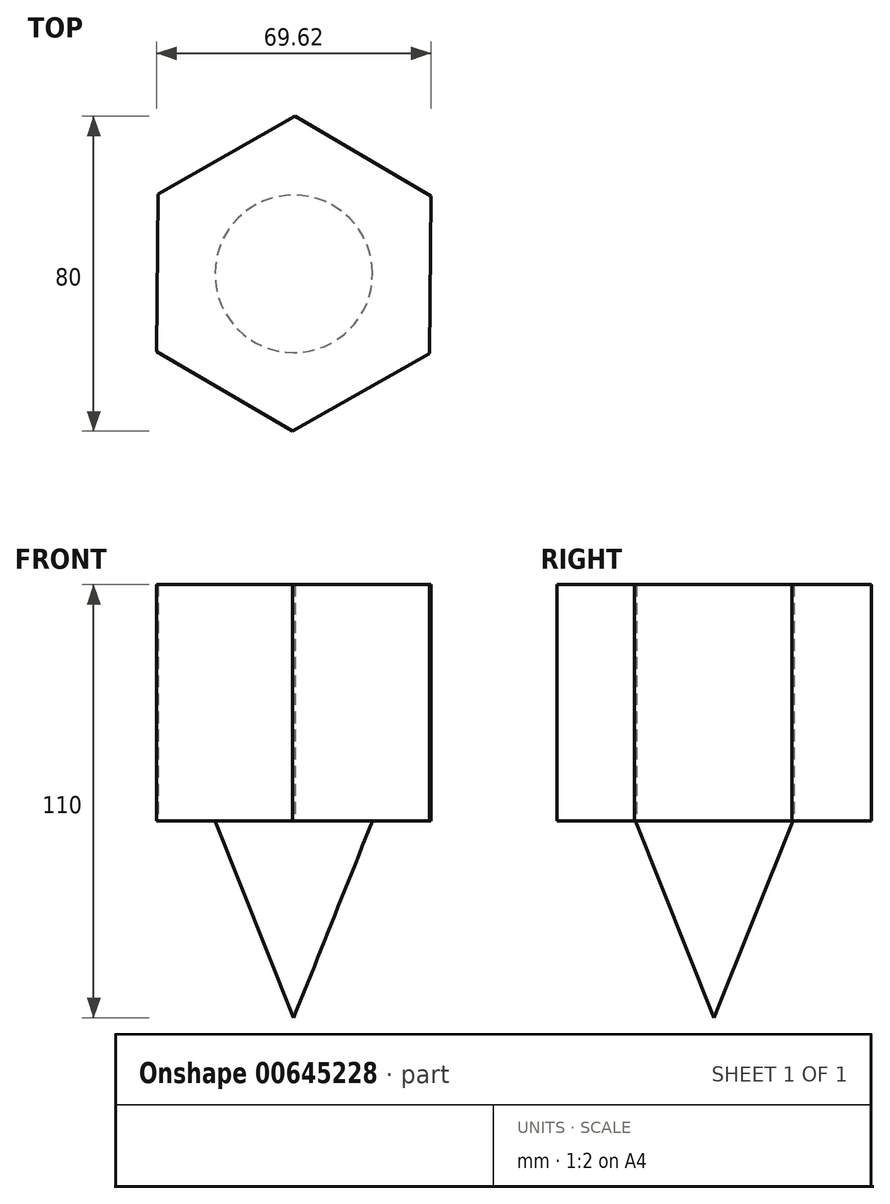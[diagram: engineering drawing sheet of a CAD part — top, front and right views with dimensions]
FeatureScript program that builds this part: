
annotation { "Feature Type Name" : "Feature", "Feature Type Description" : "" }
export const myFeature = defineFeature(function(context is Context, id is Id, definition is map)
    precondition{}
    {
        {
            var Q0;
            Q0=qCreatedBy(makeId("Top.planeOp"),FACE);
            var sketch = newSketch(context, id + "F0", { "sketchPlane" : qUnion([Q0])});
            skCircle(sketch, "E0.cCircle", {"center": v(0, 0) * mm, "radius": 34.64 * mm, "construction": true});
            skLineSegment(sketch, "E0.0", {"start": v(34.47, -20.3) * mm, "end": v(-0.34, -40) * mm});
            skLineSegment(sketch, "E0.1", {"start": v(-0.34, -40) * mm, "end": v(-34.8, -19.7) * mm});
            skLineSegment(sketch, "E0.2", {"start": v(-34.8, -19.7) * mm, "end": v(-34.47, 20.3) * mm});
            skLineSegment(sketch, "E0.3", {"start": v(-34.47, 20.3) * mm, "end": v(0.34, 40) * mm});
            skLineSegment(sketch, "E0.4", {"start": v(0.34, 40) * mm, "end": v(34.8, 19.7) * mm});
            skLineSegment(sketch, "E0.5", {"start": v(34.8, 19.7) * mm, "end": v(34.47, -20.3) * mm});
            skPoint(sketch, "E0.0.midPoint", {"position": v(17.07, -30.15) * mm});
            skSolve(sketch);
        }
        {
            var Q0;
            Q0=makeQuery(id+"F0.imprint","IMPRINT",FACE,{"disambiguationData":[TD([[makeQuery(id+"F0.imprint","IMPRINT",EDGE,{"derivedFrom":sQuery(id+"F0.wireOp",EDGE,"E0.0")}),-1.0]])]});
            extrude(context, id + "F1", {"entities" : qUnion([Q0]), "depth" : 60 * mm, "offsetDistance" : 25.4 * mm});
        }
        {
            var Q0;
            Q0=qCreatedBy(makeId("Right.planeOp"),FACE);
            var sketch = newSketch(context, id + "F2", { "sketchPlane" : qUnion([Q0])});
            skLineSegment(sketch, "E1", {"start": v(0, 0) * mm, "end": v(0, -50) * mm});
            skLineSegment(sketch, "E2", {"start": v(0, 0) * mm, "end": v(20, 0) * mm});
            skLineSegment(sketch, "E3", {"start": v(20, 0) * mm, "end": v(0, -50) * mm});
            skSolve(sketch);
        }
        {
            var Q0;
            Q0=makeQuery(id+"F2.imprint","IMPRINT",FACE,{"disambiguationData":[TD([[makeQuery(id+"F2.imprint","IMPRINT",EDGE,{"derivedFrom":sQuery(id+"F2.wireOp",EDGE,"E1")}),1.0]])]});
            var Q1;
            Q1=sQuery(id+"F2.wireOp",EDGE,"E1");
            revolve(context, id + "F3", {"operationType" : NewBodyOperationType.ADD, "entities" : qUnion([Q0]), "axis" : qUnion([Q1]), "revolveType" : RevolveType.FULL});
        }
    });
